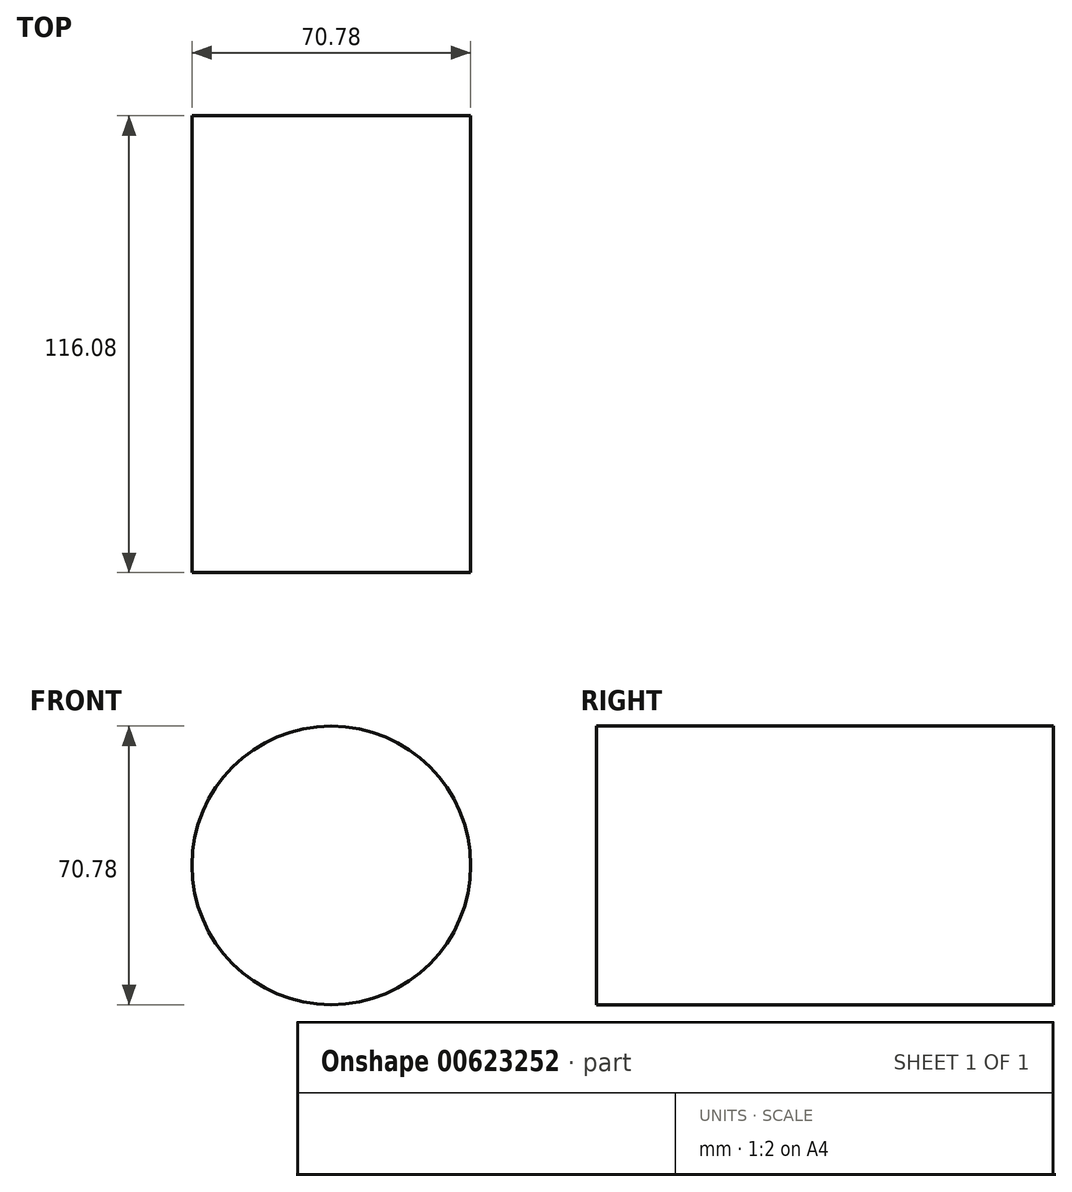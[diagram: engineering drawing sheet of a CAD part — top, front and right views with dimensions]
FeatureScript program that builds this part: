
annotation { "Feature Type Name" : "Feature", "Feature Type Description" : "" }
export const myFeature = defineFeature(function(context is Context, id is Id, definition is map)
    precondition{}
    {
        {
            var Q0;
            Q0=qCreatedBy(makeId("Front.planeOp"),FACE);
            var sketch = newSketch(context, id + "F0", { "sketchPlane" : qUnion([Q0])});
            skCircle(sketch, "E0", {"center": v(0, 0) * mm, "radius": 35.4 * mm});
            skSolve(sketch);
        }
        {
            var Q0;
            Q0=makeQuery(id+"F0.imprint","IMPRINT",FACE,{"disambiguationData":[TD([[makeQuery(id+"F0.imprint","IMPRINT",EDGE,{"derivedFrom":sQuery(id+"F0.wireOp",EDGE,"E0")}),1.0]])]});
            extrude(context, id + "F1", {"entities" : qUnion([Q0]), "depth" : 116.08 * mm, "offsetDistance" : 25.4 * mm});
        }
    });
